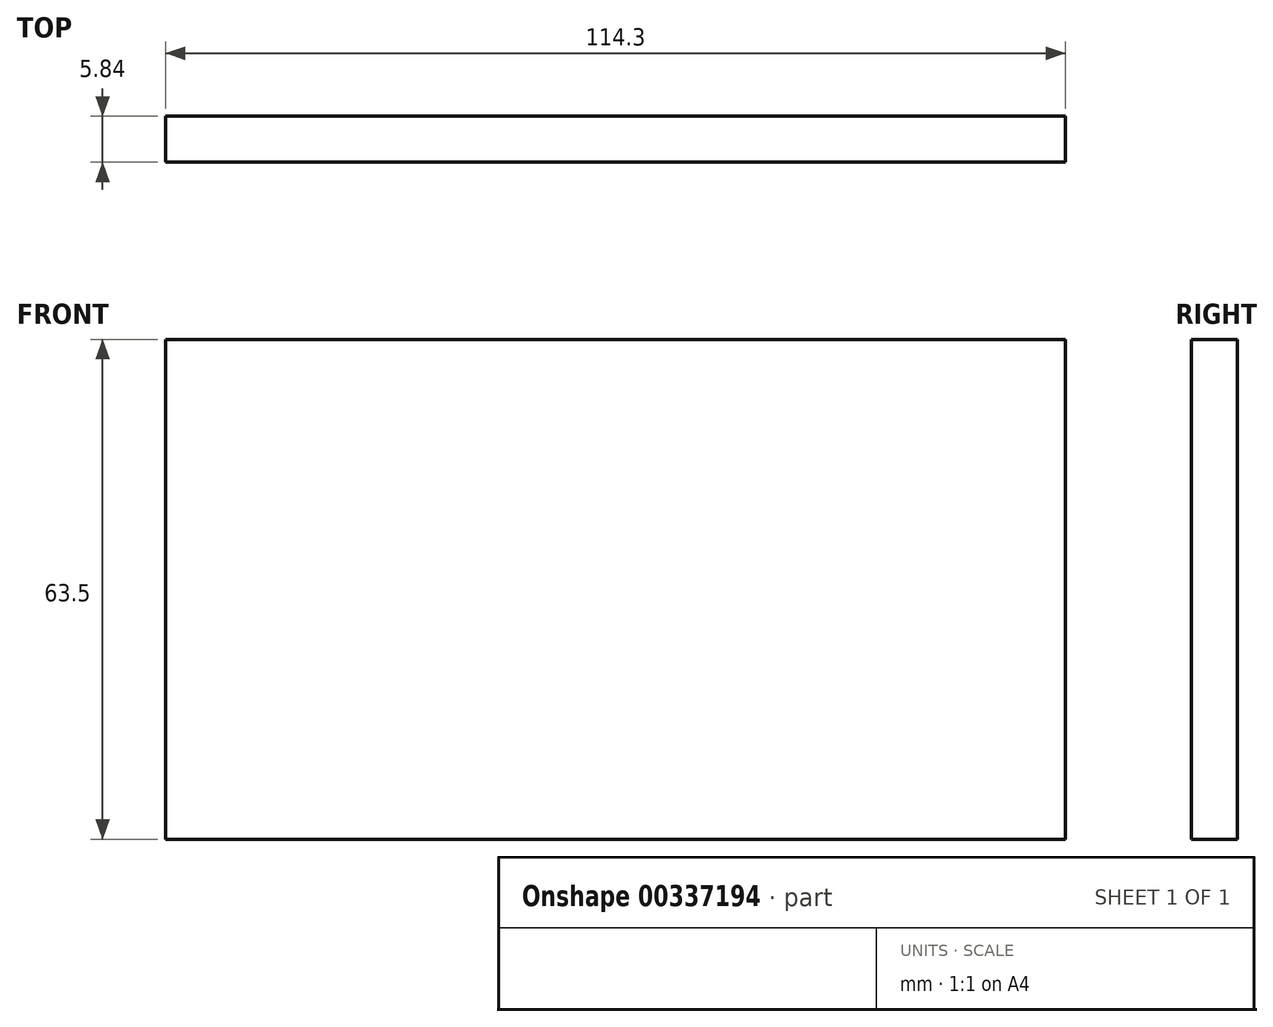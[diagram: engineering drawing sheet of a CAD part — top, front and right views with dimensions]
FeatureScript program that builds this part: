
annotation { "Feature Type Name" : "Feature", "Feature Type Description" : "" }
export const myFeature = defineFeature(function(context is Context, id is Id, definition is map)
    precondition{}
    {
        {
            var Q0;
            Q0=qCreatedBy(makeId("Front.planeOp"),FACE);
            var sketch = newSketch(context, id + "F0", { "sketchPlane" : qUnion([Q0])});
            skLineSegment(sketch, "E0.bottom", {"start": v(-57.15, 31.75) * mm, "end": v(57.15, 31.75) * mm});
            skLineSegment(sketch, "E0.top", {"start": v(-57.15, -31.75) * mm, "end": v(57.15, -31.75) * mm});
            skLineSegment(sketch, "E0.left", {"start": v(-57.15, 31.75) * mm, "end": v(-57.15, -31.75) * mm});
            skLineSegment(sketch, "E0.right", {"start": v(57.15, 31.75) * mm, "end": v(57.15, -31.75) * mm});
            skPoint(sketch, "E0.middle", {"position": v(0, 0) * mm});
            skSolve(sketch);
        }
        {
            var Q0;
            Q0=makeQuery(id+"F0.imprint","IMPRINT",FACE,{"disambiguationData":[TD([[makeQuery(id+"F0.imprint","IMPRINT",EDGE,{"derivedFrom":sQuery(id+"F0.wireOp",EDGE,"E0.bottom")}),-1.0]])]});
            extrude(context, id + "F1", {"entities" : qUnion([Q0]), "depth" : 5.84 * mm});
        }
    });
